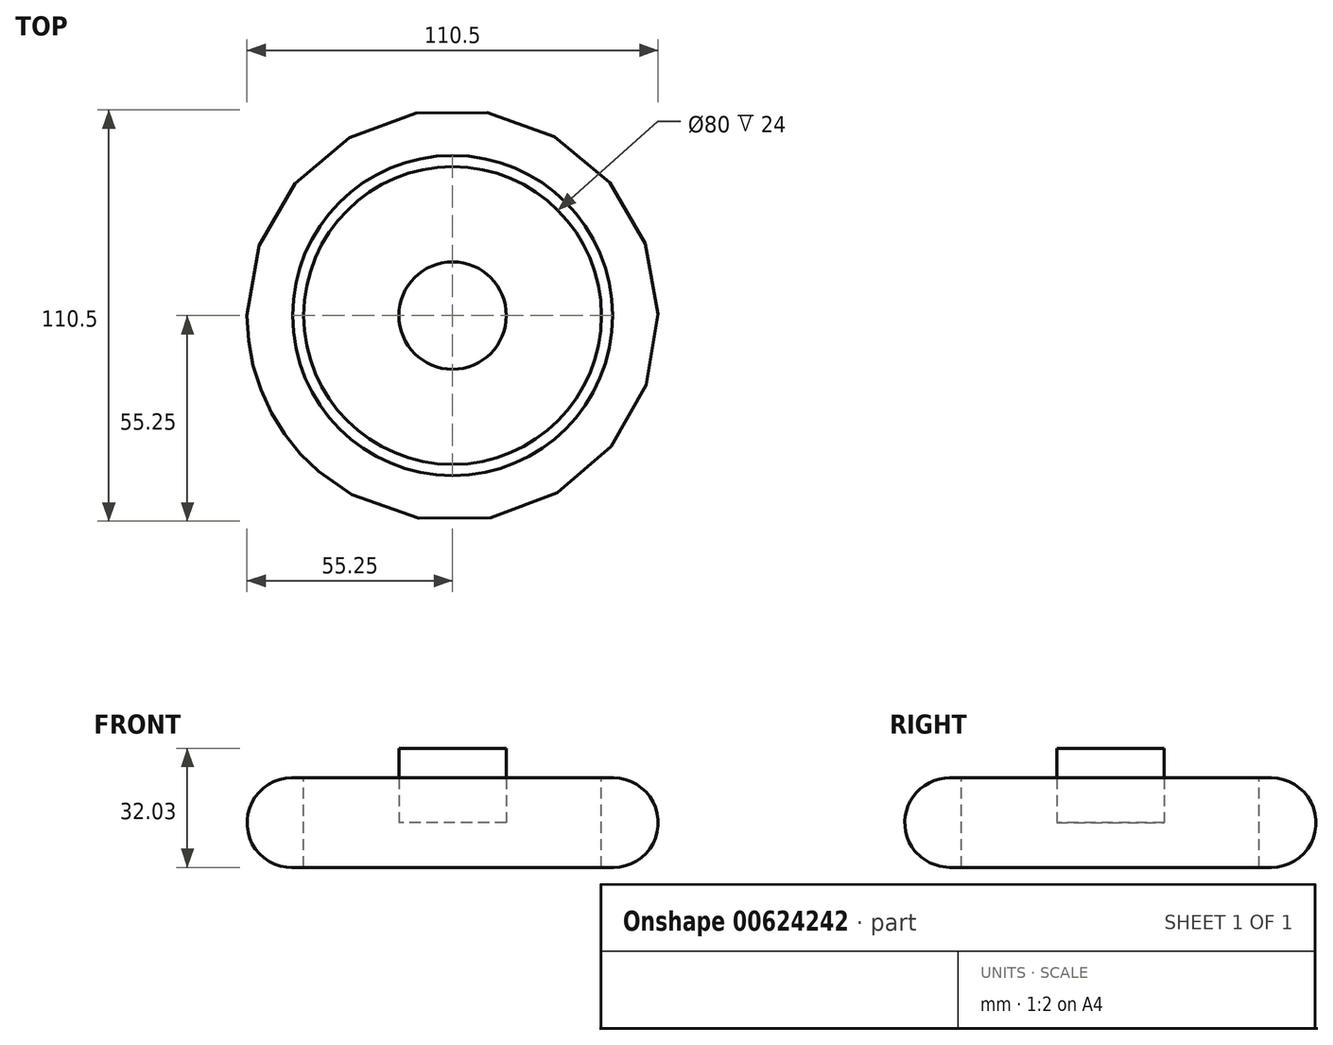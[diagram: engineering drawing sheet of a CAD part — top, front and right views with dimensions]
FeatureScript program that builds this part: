
annotation { "Feature Type Name" : "Feature", "Feature Type Description" : "" }
export const myFeature = defineFeature(function(context is Context, id is Id, definition is map)
    precondition{}
    {
        {
            var Q0;
            Q0=qCreatedBy(makeId("Top.planeOp"),FACE);
            var sketch = newSketch(context, id + "F0", { "sketchPlane" : qUnion([Q0])});
            skCircle(sketch, "E0", {"center": v(0, 0) * mm, "radius": 40 * mm});
            skSolve(sketch);
        }
        {
            var Q0;
            Q0=qCreatedBy(makeId("Front.planeOp"),FACE);
            var sketch = newSketch(context, id + "F1", { "sketchPlane" : qUnion([Q0])});
            skArc(sketch, "E1", {"start": v(-43, 12.03) * mm, "mid": v(-55.25, 0) * mm, "end": v(-43, -12.03) * mm});
            skLineSegment(sketch, "E2", {"start": v(-43, 12.03) * mm, "end": v(-40, 12.03) * mm});
            skLineSegment(sketch, "E3", {"start": v(-40, 12.03) * mm, "end": v(-40, -11.97) * mm});
            skLineSegment(sketch, "E4", {"start": v(-40, -11.97) * mm, "end": v(-43, -12.03) * mm});
            skSolve(sketch);
        }
        {
            var Q0;
            Q0=makeQuery(id+"F1.imprint","IMPRINT",FACE,{"disambiguationData":[TD([[makeQuery(id+"F1.imprint","IMPRINT",EDGE,{"derivedFrom":sQuery(id+"F1.wireOp",EDGE,"E1")}),1.0]])]});
            var Q1;
            Q1=sQuery(id+"F0.wireOp",EDGE,"E0");
            sweep(context, id + "F2", {"profiles" : qUnion([Q0]), "path" : qUnion([Q1])});
        }
        {
            var Q0;
            Q0=qCreatedBy(makeId("Top.planeOp"),FACE);
            var sketch = newSketch(context, id + "F3", { "sketchPlane" : qUnion([Q0])});
            skCircle(sketch, "E5", {"center": v(0, 0) * mm, "radius": 14.43 * mm});
            skSolve(sketch);
        }
        {
            var Q0;
            Q0 = qSketchRegion(id + "F3", true);
            extrude(context, id + "F4", {"entities" : qUnion([Q0]), "depth" : 20 * mm, "offsetDistance" : 25 * mm});
        }
        {
            var Q0;
            Q0=qCreatedBy(makeId("Top.planeOp"),FACE);
            var sketch = newSketch(context, id + "F5", { "sketchPlane" : qUnion([Q0])});
            skLineSegment(sketch, "E6", {"start": v(-9.16, 11.75) * mm, "end": v(-26.07, 32.23) * mm});
            skLineSegment(sketch, "E7", {"start": v(0, 14.84) * mm, "end": v(0, 42) * mm});
            skLineSegment(sketch, "E8", {"start": v(9.9, 10.56) * mm, "end": v(26.57, 31.52) * mm});
            skLineSegment(sketch, "E9", {"start": v(13.74, 3.82) * mm, "end": v(39.52, 6.1) * mm});
            skLineSegment(sketch, "E10", {"start": v(11.76, -6.94) * mm, "end": v(33.28, -20.54) * mm});
            skLineSegment(sketch, "E11", {"start": v(4.67, -14.3) * mm, "end": v(12.89, -38.1) * mm});
            skLineSegment(sketch, "E12", {"start": v(-5.24, -13.46) * mm, "end": v(-16.85, -34.13) * mm});
            skLineSegment(sketch, "E13", {"start": v(-16.85, -34.13) * mm, "end": v(-18.28, -36.68) * mm});
            skLineSegment(sketch, "E14", {"start": v(-13.17, -6.94) * mm, "end": v(-36.4, -16.57) * mm});
            skLineSegment(sketch, "E15", {"start": v(-14.87, 2.7) * mm, "end": v(-38.67, 8.07) * mm});
            skSolve(sketch);
        }
        {
            var Q0;
            Q0=sQuery(id+"F5.wireOp",EDGE,"E6");
            var Q1;
            Q1=sQuery(id+"F5.wireOp",EDGE,"E15");
            var Q2;
            Q2=sQuery(id+"F5.wireOp",EDGE,"E7");
            var Q3;
            Q3=sQuery(id+"F5.wireOp",EDGE,"E8");
            var Q4;
            Q4=sQuery(id+"F5.wireOp",EDGE,"E9");
            var Q5;
            Q5=sQuery(id+"F5.wireOp",EDGE,"E10");
            var Q6;
            Q6=sQuery(id+"F5.wireOp",EDGE,"E11");
            var Q7;
            Q7=sQuery(id+"F5.wireOp",EDGE,"E12");
            var Q8;
            Q8=sQuery(id+"F5.wireOp",EDGE,"E14");
            extrude(context, id + "F6", {"bodyType" : ToolBodyType.SURFACE, "surfaceEntities" : qUnion([Q0, Q1, Q2, Q3, Q4, Q5, Q6, Q7, Q8]), "depth" : 25 * mm, "offsetDistance" : 25 * mm});
        }
    });
